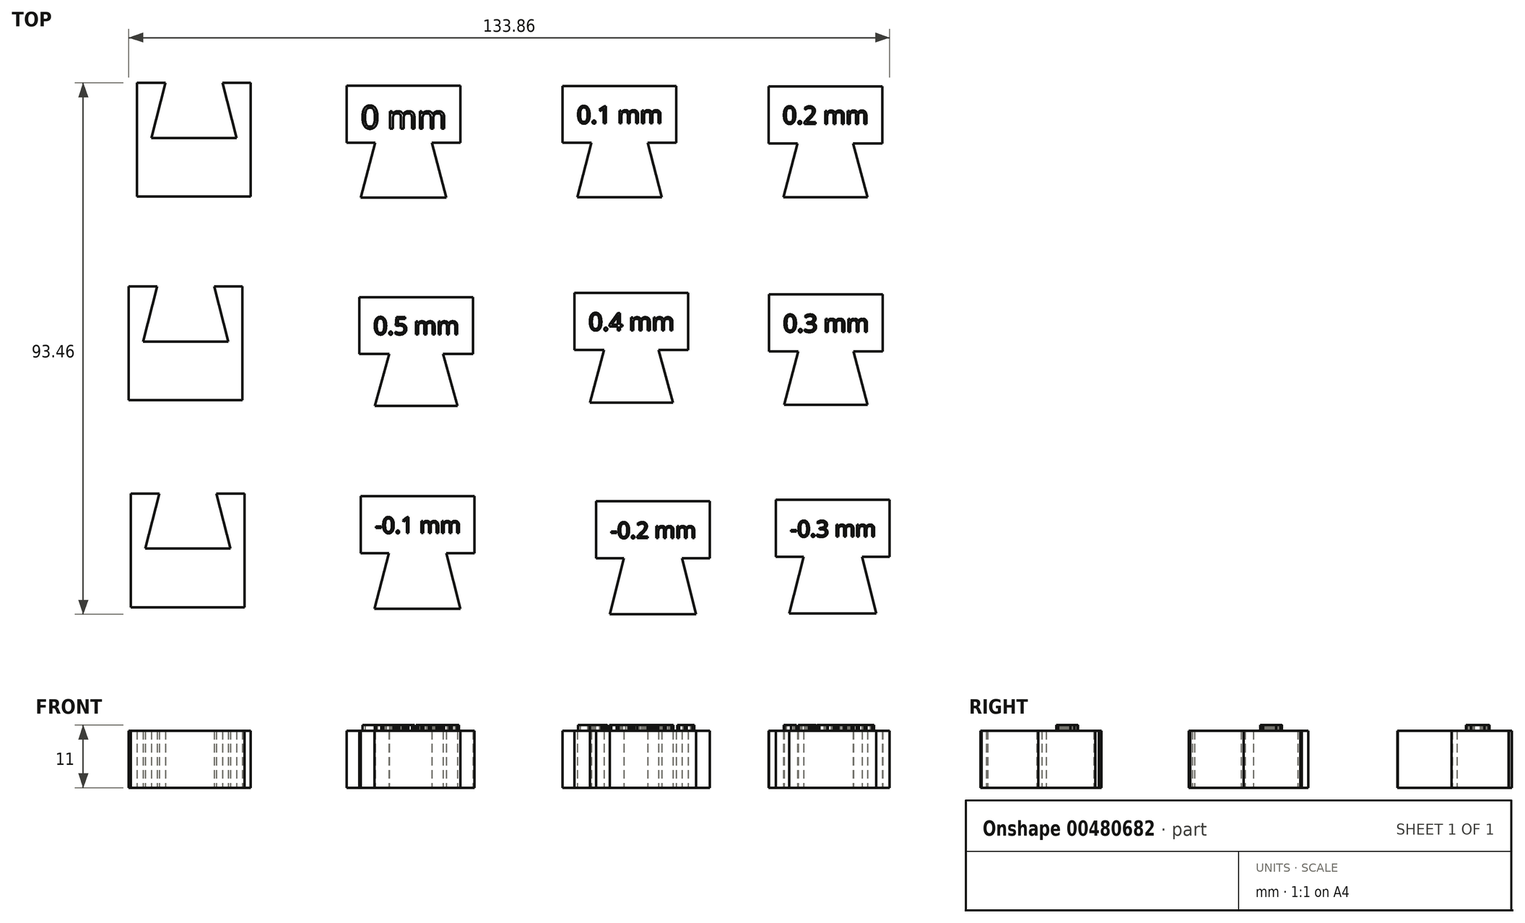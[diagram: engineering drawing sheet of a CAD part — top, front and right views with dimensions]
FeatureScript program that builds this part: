
annotation { "Feature Type Name" : "Feature", "Feature Type Description" : "" }
export const myFeature = defineFeature(function(context is Context, id is Id, definition is map)
    precondition{}
    {
        {
            var Q0;
            Q0=qCreatedBy(makeId("Top.planeOp"),FACE);
            var sketch = newSketch(context, id + "F0", { "sketchPlane" : qUnion([Q0])});
            skLineSegment(sketch, "E0", {"start": v(-59.45, 43.5) * mm, "end": v(-59.45, 23.5) * mm});
            skLineSegment(sketch, "E1", {"start": v(-59.45, 23.5) * mm, "end": v(-39.45, 23.5) * mm});
            skLineSegment(sketch, "E2", {"start": v(-39.45, 23.5) * mm, "end": v(-39.45, 43.5) * mm});
            skLineSegment(sketch, "E3", {"start": v(-39.45, 43.5) * mm, "end": v(-44.45, 43.5) * mm});
            skLineSegment(sketch, "E4", {"start": v(-44.45, 43.5) * mm, "end": v(-41.95, 33.82) * mm});
            skLineSegment(sketch, "E5", {"start": v(-41.95, 33.82) * mm, "end": v(-56.95, 33.82) * mm});
            skLineSegment(sketch, "E6", {"start": v(-56.95, 33.82) * mm, "end": v(-54.45, 43.5) * mm});
            skLineSegment(sketch, "E7", {"start": v(-54.45, 43.5) * mm, "end": v(-59.45, 43.5) * mm});
            skLineSegment(sketch, "E8", {"start": v(-17.58, 33.01) * mm, "end": v(-20.08, 23.33) * mm});
            skLineSegment(sketch, "E9", {"start": v(-20.08, 23.33) * mm, "end": v(-5.08, 23.33) * mm});
            skLineSegment(sketch, "E10", {"start": v(-5.08, 23.33) * mm, "end": v(-7.58, 33.01) * mm});
            skLineSegment(sketch, "E11", {"start": v(-7.58, 33.01) * mm, "end": v(-2.58, 33.01) * mm});
            skLineSegment(sketch, "E12", {"start": v(-2.58, 33.01) * mm, "end": v(-2.58, 43.01) * mm});
            skLineSegment(sketch, "E13", {"start": v(-2.58, 43.01) * mm, "end": v(-22.58, 43.01) * mm});
            skLineSegment(sketch, "E14", {"start": v(-22.58, 43.01) * mm, "end": v(-22.58, 33.01) * mm});
            skLineSegment(sketch, "E15", {"start": v(-22.58, 33.01) * mm, "end": v(-17.58, 33.01) * mm});
            skLineSegment(sketch, "E16", {"start": v(20.48, 32.96) * mm, "end": v(17.98, 23.38) * mm});
            skLineSegment(sketch, "E17", {"start": v(17.98, 23.38) * mm, "end": v(32.88, 23.38) * mm});
            skLineSegment(sketch, "E18", {"start": v(32.88, 23.38) * mm, "end": v(30.38, 32.96) * mm});
            skLineSegment(sketch, "E19", {"start": v(30.38, 32.96) * mm, "end": v(35.43, 32.96) * mm});
            skLineSegment(sketch, "E20", {"start": v(35.43, 32.96) * mm, "end": v(35.43, 42.96) * mm});
            skLineSegment(sketch, "E21", {"start": v(35.43, 42.96) * mm, "end": v(15.43, 42.96) * mm});
            skLineSegment(sketch, "E22", {"start": v(15.43, 42.96) * mm, "end": v(15.43, 32.96) * mm});
            skLineSegment(sketch, "E23", {"start": v(15.43, 32.96) * mm, "end": v(20.48, 32.96) * mm});
            skLineSegment(sketch, "E24", {"start": v(56.73, 32.9) * mm, "end": v(54.23, 23.42) * mm});
            skLineSegment(sketch, "E25", {"start": v(54.23, 23.42) * mm, "end": v(69.03, 23.42) * mm});
            skLineSegment(sketch, "E26", {"start": v(69.03, 23.42) * mm, "end": v(66.53, 32.9) * mm});
            skLineSegment(sketch, "E27", {"start": v(66.53, 32.9) * mm, "end": v(71.63, 32.9) * mm});
            skLineSegment(sketch, "E28", {"start": v(71.63, 32.9) * mm, "end": v(71.63, 42.9) * mm});
            skLineSegment(sketch, "E29", {"start": v(71.63, 42.9) * mm, "end": v(51.63, 42.9) * mm});
            skLineSegment(sketch, "E30", {"start": v(51.63, 42.9) * mm, "end": v(51.63, 32.9) * mm});
            skLineSegment(sketch, "E31", {"start": v(51.63, 32.9) * mm, "end": v(56.73, 32.9) * mm});
            skLineSegment(sketch, "E32", {"start": v(56.88, -3.71) * mm, "end": v(54.38, -13.08) * mm});
            skLineSegment(sketch, "E33", {"start": v(54.38, -13.08) * mm, "end": v(69.08, -13.08) * mm});
            skLineSegment(sketch, "E34", {"start": v(69.08, -13.08) * mm, "end": v(66.58, -3.71) * mm});
            skLineSegment(sketch, "E35", {"start": v(66.58, -3.71) * mm, "end": v(71.73, -3.71) * mm});
            skLineSegment(sketch, "E36", {"start": v(71.73, -3.71) * mm, "end": v(71.73, 6.29) * mm});
            skLineSegment(sketch, "E37", {"start": v(71.73, 6.29) * mm, "end": v(51.73, 6.29) * mm});
            skLineSegment(sketch, "E38", {"start": v(51.73, 6.29) * mm, "end": v(51.73, -3.71) * mm});
            skLineSegment(sketch, "E39", {"start": v(51.73, -3.71) * mm, "end": v(56.88, -3.71) * mm});
            skLineSegment(sketch, "E40", {"start": v(22.7, -3.44) * mm, "end": v(20.2, -12.71) * mm});
            skLineSegment(sketch, "E41", {"start": v(20.2, -12.71) * mm, "end": v(34.8, -12.71) * mm});
            skLineSegment(sketch, "E42", {"start": v(34.8, -12.71) * mm, "end": v(32.3, -3.44) * mm});
            skLineSegment(sketch, "E43", {"start": v(32.3, -3.44) * mm, "end": v(37.5, -3.44) * mm});
            skLineSegment(sketch, "E44", {"start": v(37.5, -3.44) * mm, "end": v(37.5, 6.56) * mm});
            skLineSegment(sketch, "E45", {"start": v(37.5, 6.56) * mm, "end": v(17.5, 6.56) * mm});
            skLineSegment(sketch, "E46", {"start": v(17.5, 6.56) * mm, "end": v(17.5, -3.44) * mm});
            skLineSegment(sketch, "E47", {"start": v(17.5, -3.44) * mm, "end": v(22.7, -3.44) * mm});
            skLineSegment(sketch, "E48", {"start": v(-15.1, -4.16) * mm, "end": v(-17.6, -13.32) * mm});
            skLineSegment(sketch, "E49", {"start": v(-17.6, -13.32) * mm, "end": v(-3.1, -13.32) * mm});
            skLineSegment(sketch, "E50", {"start": v(-3.1, -13.32) * mm, "end": v(-5.6, -4.16) * mm});
            skLineSegment(sketch, "E51", {"start": v(-5.6, -4.16) * mm, "end": v(-0.35, -4.16) * mm});
            skLineSegment(sketch, "E52", {"start": v(-0.35, -4.16) * mm, "end": v(-0.35, 5.84) * mm});
            skLineSegment(sketch, "E53", {"start": v(-0.35, 5.84) * mm, "end": v(-20.35, 5.84) * mm});
            skLineSegment(sketch, "E54", {"start": v(-20.35, 5.84) * mm, "end": v(-20.35, -4.16) * mm});
            skLineSegment(sketch, "E55", {"start": v(-20.35, -4.16) * mm, "end": v(-15.1, -4.16) * mm});
            skLineSegment(sketch, "E56", {"start": v(-15.16, -39.18) * mm, "end": v(-17.66, -48.97) * mm});
            skLineSegment(sketch, "E57", {"start": v(-17.66, -48.97) * mm, "end": v(-2.56, -48.97) * mm});
            skLineSegment(sketch, "E58", {"start": v(-2.56, -48.97) * mm, "end": v(-5.06, -39.18) * mm});
            skLineSegment(sketch, "E59", {"start": v(-5.06, -39.18) * mm, "end": v(-0.1, -39.18) * mm});
            skLineSegment(sketch, "E60", {"start": v(-0.1, -39.18) * mm, "end": v(-0.1, -29.18) * mm});
            skLineSegment(sketch, "E61", {"start": v(-0.1, -29.18) * mm, "end": v(-20.1, -29.18) * mm});
            skLineSegment(sketch, "E62", {"start": v(-20.1, -29.18) * mm, "end": v(-20.1, -39.18) * mm});
            skLineSegment(sketch, "E63", {"start": v(-20.1, -39.18) * mm, "end": v(-15.16, -39.18) * mm});
            skLineSegment(sketch, "E64", {"start": v(26.19, -40.07) * mm, "end": v(23.69, -49.96) * mm});
            skLineSegment(sketch, "E65", {"start": v(23.69, -49.96) * mm, "end": v(38.89, -49.96) * mm});
            skLineSegment(sketch, "E66", {"start": v(38.89, -49.96) * mm, "end": v(36.39, -40.07) * mm});
            skLineSegment(sketch, "E67", {"start": v(36.39, -40.07) * mm, "end": v(41.29, -40.07) * mm});
            skLineSegment(sketch, "E68", {"start": v(41.29, -40.07) * mm, "end": v(41.29, -30.07) * mm});
            skLineSegment(sketch, "E69", {"start": v(41.29, -30.07) * mm, "end": v(21.29, -30.07) * mm});
            skLineSegment(sketch, "E70", {"start": v(21.29, -30.07) * mm, "end": v(21.29, -40.07) * mm});
            skLineSegment(sketch, "E71", {"start": v(21.29, -40.07) * mm, "end": v(26.19, -40.07) * mm});
            skLineSegment(sketch, "E72", {"start": v(57.8, -39.82) * mm, "end": v(55.3, -49.8) * mm});
            skLineSegment(sketch, "E73", {"start": v(55.3, -49.8) * mm, "end": v(70.6, -49.8) * mm});
            skLineSegment(sketch, "E74", {"start": v(70.6, -49.8) * mm, "end": v(68.1, -39.82) * mm});
            skLineSegment(sketch, "E75", {"start": v(68.1, -39.82) * mm, "end": v(72.95, -39.82) * mm});
            skLineSegment(sketch, "E76", {"start": v(72.95, -39.82) * mm, "end": v(72.95, -29.82) * mm});
            skLineSegment(sketch, "E77", {"start": v(72.95, -29.82) * mm, "end": v(52.95, -29.82) * mm});
            skLineSegment(sketch, "E78", {"start": v(52.95, -29.82) * mm, "end": v(52.95, -39.82) * mm});
            skLineSegment(sketch, "E79", {"start": v(52.95, -39.82) * mm, "end": v(57.8, -39.82) * mm});
            skLineSegment(sketch, "E80", {"start": v(-60.9, 7.7) * mm, "end": v(-60.9, -12.3) * mm});
            skLineSegment(sketch, "E81", {"start": v(-60.9, -12.3) * mm, "end": v(-40.9, -12.3) * mm});
            skLineSegment(sketch, "E82", {"start": v(-40.9, -12.3) * mm, "end": v(-40.9, 7.7) * mm});
            skLineSegment(sketch, "E83", {"start": v(-40.9, 7.7) * mm, "end": v(-45.9, 7.7) * mm});
            skLineSegment(sketch, "E84", {"start": v(-45.9, 7.7) * mm, "end": v(-43.4, -1.98) * mm});
            skLineSegment(sketch, "E85", {"start": v(-43.4, -1.98) * mm, "end": v(-58.4, -1.98) * mm});
            skLineSegment(sketch, "E86", {"start": v(-58.4, -1.98) * mm, "end": v(-55.9, 7.7) * mm});
            skLineSegment(sketch, "E87", {"start": v(-55.9, 7.7) * mm, "end": v(-60.9, 7.7) * mm});
            skLineSegment(sketch, "E88", {"start": v(-60.52, -28.73) * mm, "end": v(-60.52, -48.73) * mm});
            skLineSegment(sketch, "E89", {"start": v(-60.52, -48.73) * mm, "end": v(-40.52, -48.73) * mm});
            skLineSegment(sketch, "E90", {"start": v(-40.52, -48.73) * mm, "end": v(-40.52, -28.73) * mm});
            skLineSegment(sketch, "E91", {"start": v(-40.52, -28.73) * mm, "end": v(-45.52, -28.73) * mm});
            skLineSegment(sketch, "E92", {"start": v(-45.52, -28.73) * mm, "end": v(-43.02, -38.41) * mm});
            skLineSegment(sketch, "E93", {"start": v(-43.02, -38.41) * mm, "end": v(-58.02, -38.41) * mm});
            skLineSegment(sketch, "E94", {"start": v(-58.02, -38.41) * mm, "end": v(-55.52, -28.73) * mm});
            skLineSegment(sketch, "E95", {"start": v(-55.52, -28.73) * mm, "end": v(-60.52, -28.73) * mm});
            skSolve(sketch);
        }
        {
            var Q0;
            Q0 = qSketchRegion(id + "F0", true);
            extrude(context, id + "F1", {"entities" : qUnion([Q0]), "depth" : 10 * mm});
        }
        {
            var Q0;
            Q0=makeQuery(id+"F1.opExtrude","CAP_FACE",FACE,{"disambiguationData":[OSD([sQuery(id+"F0.wireOp",EDGE,"E8"),sQuery(id+"F0.wireOp",EDGE,"E9"),sQuery(id+"F0.wireOp",EDGE,"E10"),sQuery(id+"F0.wireOp",EDGE,"E11"),sQuery(id+"F0.wireOp",EDGE,"E12"),sQuery(id+"F0.wireOp",EDGE,"E13"),sQuery(id+"F0.wireOp",EDGE,"E14"),sQuery(id+"F0.wireOp",EDGE,"E15")])],"isStart":false});
            var sketch = newSketch(context, id + "F2", { "sketchPlane" : qUnion([Q0])});
            skText(sketch, "E96", { "text": "0 mm", "fontName": "OpenSans-Regular.ttf"});
            const initialGuessF2  = {"E96": [-0.02008, 0.03548, 1, 0, 0.00404]};
            skSetInitialGuess(sketch, initialGuessF2);
            skSolve(sketch);
        }
        {
            var Q0;
            Q0 = qSketchRegion(id + "F2", true);
            extrude(context, id + "F3", {"entities" : qUnion([Q0]), "operationType" : NewBodyOperationType.ADD, "depth" : 1 * mm});
        }
        {
            var Q0;
            Q0=makeQuery(id+"F1.opExtrude","CAP_FACE",FACE,{"disambiguationData":[OSD([sQuery(id+"F0.wireOp",EDGE,"E16"),sQuery(id+"F0.wireOp",EDGE,"E17"),sQuery(id+"F0.wireOp",EDGE,"E18"),sQuery(id+"F0.wireOp",EDGE,"E19"),sQuery(id+"F0.wireOp",EDGE,"E20"),sQuery(id+"F0.wireOp",EDGE,"E21"),sQuery(id+"F0.wireOp",EDGE,"E22"),sQuery(id+"F0.wireOp",EDGE,"E23")])],"isStart":false});
            var sketch = newSketch(context, id + "F4", { "sketchPlane" : qUnion([Q0])});
            skText(sketch, "E97", { "text": "0.1 mm", "fontName": "OpenSans-Regular.ttf"});
            const initialGuessF4  = {"E97": [0.01793, 0.03639, 1, 0, 0.00307]};
            skSetInitialGuess(sketch, initialGuessF4);
            skSolve(sketch);
        }
        {
            var Q0;
            Q0 = qSketchRegion(id + "F4", true);
            extrude(context, id + "F5", {"entities" : qUnion([Q0]), "operationType" : NewBodyOperationType.ADD, "depth" : 1 * mm});
        }
        {
            var Q0;
            Q0=makeQuery(id+"F1.opExtrude","CAP_FACE",FACE,{"disambiguationData":[OSD([sQuery(id+"F0.wireOp",EDGE,"E24"),sQuery(id+"F0.wireOp",EDGE,"E25"),sQuery(id+"F0.wireOp",EDGE,"E26"),sQuery(id+"F0.wireOp",EDGE,"E27"),sQuery(id+"F0.wireOp",EDGE,"E28"),sQuery(id+"F0.wireOp",EDGE,"E29"),sQuery(id+"F0.wireOp",EDGE,"E30"),sQuery(id+"F0.wireOp",EDGE,"E31")])],"isStart":false});
            var sketch = newSketch(context, id + "F6", { "sketchPlane" : qUnion([Q0])});
            skText(sketch, "E98", { "text": "0.2 mm", "fontName": "OpenSans-Regular.ttf"});
            const initialGuessF6  = {"E98": [0.05413, 0.03632, 1, 0, 0.00307]};
            skSetInitialGuess(sketch, initialGuessF6);
            skSolve(sketch);
        }
        {
            var Q0;
            Q0 = qSketchRegion(id + "F6", true);
            extrude(context, id + "F7", {"entities" : qUnion([Q0]), "operationType" : NewBodyOperationType.ADD, "depth" : 1 * mm});
        }
        {
            var Q0;
            Q0=makeQuery(id+"F1.opExtrude","CAP_FACE",FACE,{"disambiguationData":[OSD([sQuery(id+"F0.wireOp",EDGE,"E48"),sQuery(id+"F0.wireOp",EDGE,"E49"),sQuery(id+"F0.wireOp",EDGE,"E50"),sQuery(id+"F0.wireOp",EDGE,"E51"),sQuery(id+"F0.wireOp",EDGE,"E52"),sQuery(id+"F0.wireOp",EDGE,"E53"),sQuery(id+"F0.wireOp",EDGE,"E54"),sQuery(id+"F0.wireOp",EDGE,"E55")])],"isStart":false});
            var sketch = newSketch(context, id + "F8", { "sketchPlane" : qUnion([Q0])});
            skText(sketch, "E99", { "text": "0.5 mm", "fontName": "OpenSans-Regular.ttf"});
            const initialGuessF8  = {"E99": [-0.01785, -0.00073, 1, 0, 0.00307]};
            skSetInitialGuess(sketch, initialGuessF8);
            skSolve(sketch);
        }
        {
            var Q0;
            Q0 = qSketchRegion(id + "F8", true);
            extrude(context, id + "F9", {"entities" : qUnion([Q0]), "operationType" : NewBodyOperationType.ADD, "depth" : 1 * mm});
        }
        {
            var Q0;
            Q0=makeQuery(id+"F1.opExtrude","CAP_FACE",FACE,{"disambiguationData":[OSD([sQuery(id+"F0.wireOp",EDGE,"E40"),sQuery(id+"F0.wireOp",EDGE,"E41"),sQuery(id+"F0.wireOp",EDGE,"E42"),sQuery(id+"F0.wireOp",EDGE,"E43"),sQuery(id+"F0.wireOp",EDGE,"E44"),sQuery(id+"F0.wireOp",EDGE,"E45"),sQuery(id+"F0.wireOp",EDGE,"E46"),sQuery(id+"F0.wireOp",EDGE,"E47")])],"isStart":false});
            var sketch = newSketch(context, id + "F10", { "sketchPlane" : qUnion([Q0])});
            skText(sketch, "E100", { "text": "0.4 mm", "fontName": "OpenSans-Regular.ttf"});
            const initialGuessF10  = {"E100": [0.02, -2e-05, 1, 0, 0.00307]};
            skSetInitialGuess(sketch, initialGuessF10);
            skSolve(sketch);
        }
        {
            var Q0;
            Q0 = qSketchRegion(id + "F10", true);
            extrude(context, id + "F11", {"entities" : qUnion([Q0]), "operationType" : NewBodyOperationType.ADD, "depth" : 1 * mm});
        }
        {
            var Q0;
            Q0=makeQuery(id+"F1.opExtrude","CAP_FACE",FACE,{"disambiguationData":[OSD([sQuery(id+"F0.wireOp",EDGE,"E32"),sQuery(id+"F0.wireOp",EDGE,"E33"),sQuery(id+"F0.wireOp",EDGE,"E34"),sQuery(id+"F0.wireOp",EDGE,"E35"),sQuery(id+"F0.wireOp",EDGE,"E36"),sQuery(id+"F0.wireOp",EDGE,"E37"),sQuery(id+"F0.wireOp",EDGE,"E38"),sQuery(id+"F0.wireOp",EDGE,"E39")])],"isStart":false});
            var sketch = newSketch(context, id + "F12", { "sketchPlane" : qUnion([Q0])});
            skText(sketch, "E101", { "text": "0.3 mm", "fontName": "OpenSans-Regular.ttf"});
            const initialGuessF12  = {"E101": [0.05423, -0.00029, 1, 0, 0.00307]};
            skSetInitialGuess(sketch, initialGuessF12);
            skSolve(sketch);
        }
        {
            var Q0;
            Q0 = qSketchRegion(id + "F12", true);
            extrude(context, id + "F13", {"entities" : qUnion([Q0]), "operationType" : NewBodyOperationType.ADD, "depth" : 1 * mm});
        }
        {
            var Q0;
            Q0=makeQuery(id+"F1.opExtrude","CAP_FACE",FACE,{"disambiguationData":[OSD([sQuery(id+"F0.wireOp",EDGE,"E56"),sQuery(id+"F0.wireOp",EDGE,"E57"),sQuery(id+"F0.wireOp",EDGE,"E58"),sQuery(id+"F0.wireOp",EDGE,"E59"),sQuery(id+"F0.wireOp",EDGE,"E60"),sQuery(id+"F0.wireOp",EDGE,"E61"),sQuery(id+"F0.wireOp",EDGE,"E62"),sQuery(id+"F0.wireOp",EDGE,"E63")])],"isStart":false});
            var sketch = newSketch(context, id + "F14", { "sketchPlane" : qUnion([Q0])});
            skText(sketch, "E102", { "text": "-0.1 mm", "fontName": "OpenSans-Regular.ttf"});
            const initialGuessF14  = {"E102": [-0.0176, -0.03568, 1, 0, 0.00282]};
            skSetInitialGuess(sketch, initialGuessF14);
            skSolve(sketch);
        }
        {
            var Q0;
            Q0 = qSketchRegion(id + "F14", true);
            extrude(context, id + "F15", {"entities" : qUnion([Q0]), "operationType" : NewBodyOperationType.ADD, "depth" : 1 * mm});
        }
        {
            var Q0;
            Q0=makeQuery(id+"F1.opExtrude","CAP_FACE",FACE,{"disambiguationData":[OSD([sQuery(id+"F0.wireOp",EDGE,"E64"),sQuery(id+"F0.wireOp",EDGE,"E65"),sQuery(id+"F0.wireOp",EDGE,"E66"),sQuery(id+"F0.wireOp",EDGE,"E67"),sQuery(id+"F0.wireOp",EDGE,"E68"),sQuery(id+"F0.wireOp",EDGE,"E69"),sQuery(id+"F0.wireOp",EDGE,"E70"),sQuery(id+"F0.wireOp",EDGE,"E71")])],"isStart":false});
            var sketch = newSketch(context, id + "F16", { "sketchPlane" : qUnion([Q0])});
            skText(sketch, "E103", { "text": "-0.2 mm", "fontName": "OpenSans-Regular.ttf"});
            const initialGuessF16  = {"E103": [0.02379, -0.03657, 1, 0, 0.00282]};
            skSetInitialGuess(sketch, initialGuessF16);
            skSolve(sketch);
        }
        {
            var Q0;
            Q0 = qSketchRegion(id + "F16", true);
            extrude(context, id + "F17", {"entities" : qUnion([Q0]), "operationType" : NewBodyOperationType.ADD, "depth" : 1 * mm});
        }
        {
            var Q0;
            Q0=makeQuery(id+"F1.opExtrude","CAP_FACE",FACE,{"disambiguationData":[OSD([sQuery(id+"F0.wireOp",EDGE,"E72"),sQuery(id+"F0.wireOp",EDGE,"E73"),sQuery(id+"F0.wireOp",EDGE,"E74"),sQuery(id+"F0.wireOp",EDGE,"E75"),sQuery(id+"F0.wireOp",EDGE,"E76"),sQuery(id+"F0.wireOp",EDGE,"E77"),sQuery(id+"F0.wireOp",EDGE,"E78"),sQuery(id+"F0.wireOp",EDGE,"E79")])],"isStart":false});
            var sketch = newSketch(context, id + "F18", { "sketchPlane" : qUnion([Q0])});
            skText(sketch, "E104", { "text": "-0.3 mm", "fontName": "OpenSans-Regular.ttf"});
            const initialGuessF18  = {"E104": [0.05545, -0.03632, 1, 0, 0.00282]};
            skSetInitialGuess(sketch, initialGuessF18);
            skSolve(sketch);
        }
        {
            var Q0;
            Q0 = qSketchRegion(id + "F18", true);
            extrude(context, id + "F19", {"entities" : qUnion([Q0]), "operationType" : NewBodyOperationType.ADD, "depth" : 1 * mm});
        }
    });
